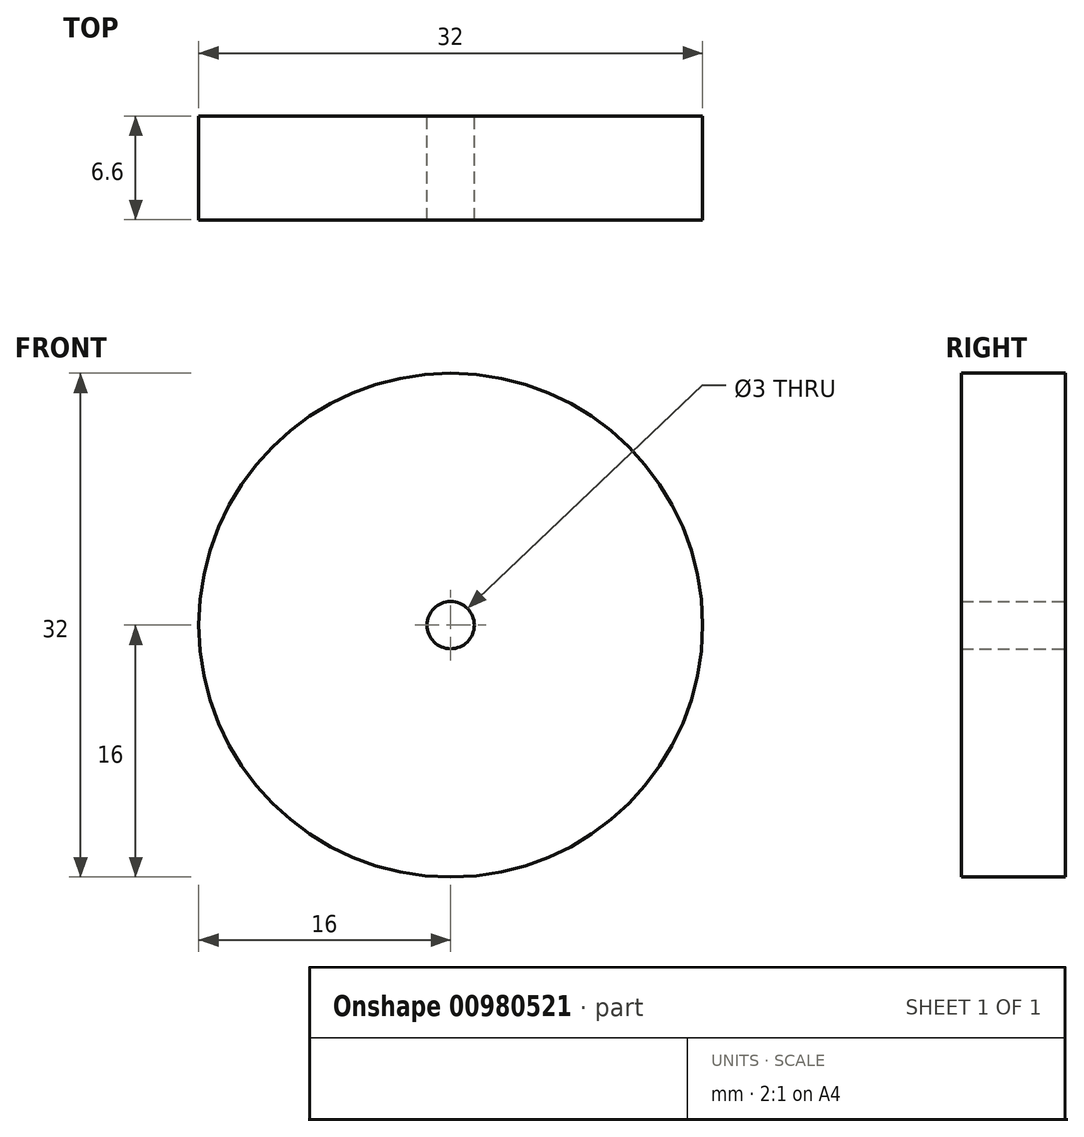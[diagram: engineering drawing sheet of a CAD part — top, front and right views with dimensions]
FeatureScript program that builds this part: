
annotation { "Feature Type Name" : "Feature", "Feature Type Description" : "" }
export const myFeature = defineFeature(function(context is Context, id is Id, definition is map)
    precondition{}
    {
        {
            var Q0;
            Q0=qCreatedBy(makeId("Front.planeOp"),FACE);
            var sketch = newSketch(context, id + "F0", { "sketchPlane" : qUnion([Q0])});
            skCircle(sketch, "E0", {"center": v(0, 0) * mm, "radius": 16 * mm});
            skCircle(sketch, "E1", {"center": v(0, 0) * mm, "radius": 1.5 * mm});
            skSolve(sketch);
        }
        {
            var Q0;
            Q0=makeQuery(id+"F0.imprint","IMPRINT",FACE,{"disambiguationData":[TD([[makeQuery(id+"F0.imprint","IMPRINT",EDGE,{"derivedFrom":sQuery(id+"F0.wireOp",EDGE,"E0")}),1.0]])]});
            extrude(context, id + "F1", {"entities" : qUnion([Q0]), "depth" : 6.6 * mm, "offsetDistance" : 25.4 * mm});
        }
    });
